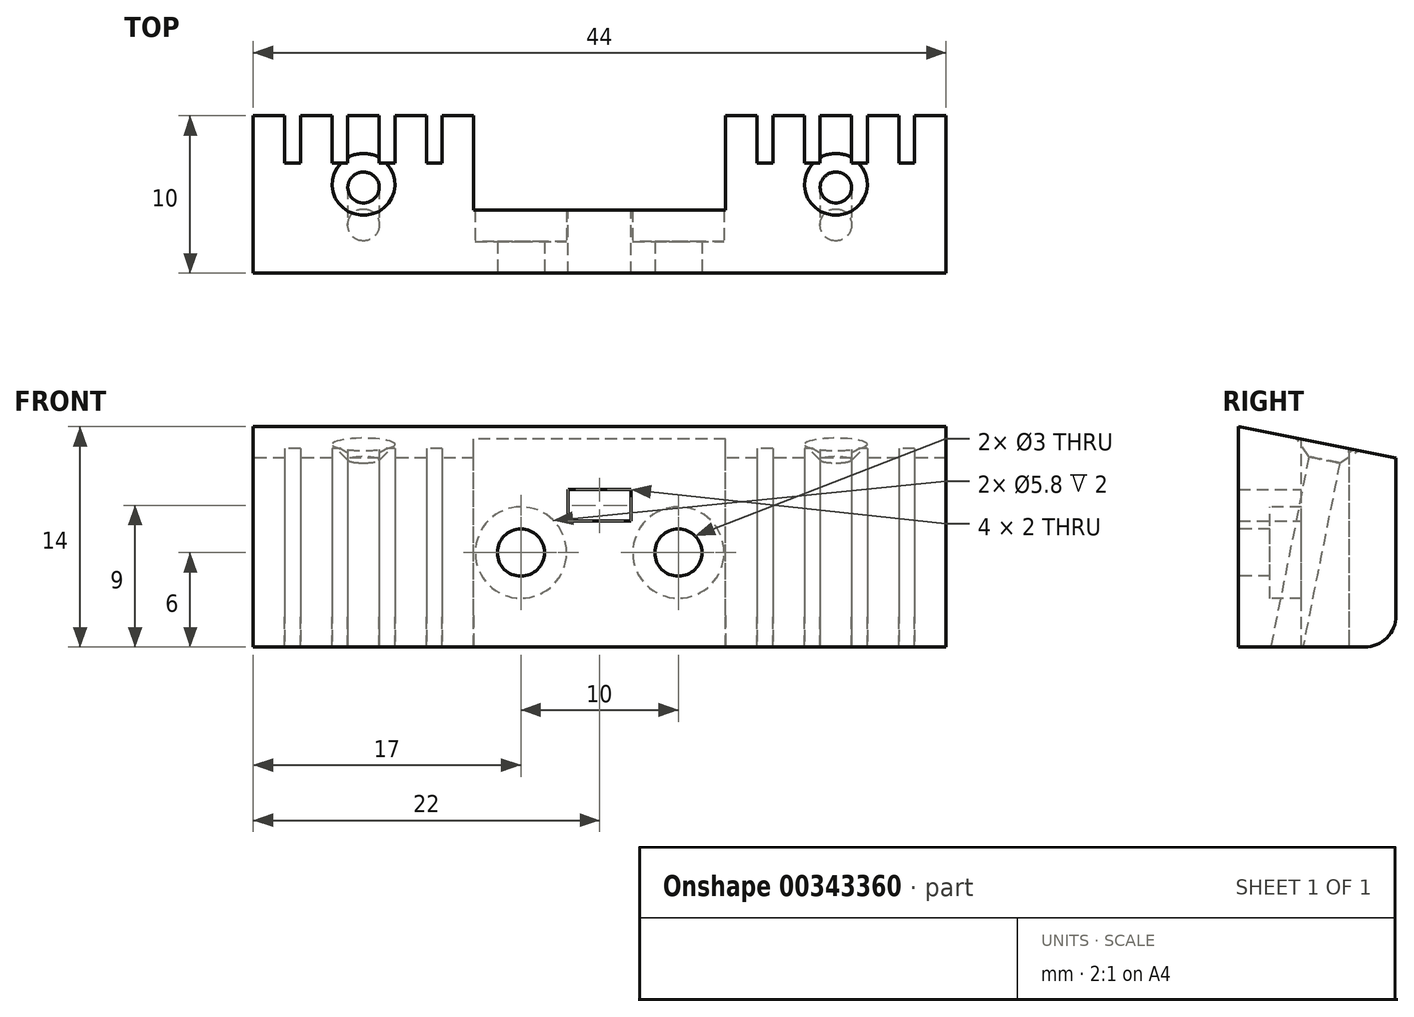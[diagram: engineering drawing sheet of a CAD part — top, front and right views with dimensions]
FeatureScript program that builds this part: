
annotation { "Feature Type Name" : "Feature", "Feature Type Description" : "" }
export const myFeature = defineFeature(function(context is Context, id is Id, definition is map)
    precondition{}
    {
        {
            var Q0;
            Q0=qCreatedBy(makeId("Right.planeOp"),FACE);
            var sketch = newSketch(context, id + "F0", { "sketchPlane" : qUnion([Q0])});
            skLineSegment(sketch, "E0.bottom", {"start": v(5, -7) * mm, "end": v(-5, -7) * mm});
            skLineSegment(sketch, "E0.top", {"start": v(5, 7) * mm, "end": v(-5, 7) * mm});
            skLineSegment(sketch, "E0.left", {"start": v(5, -7) * mm, "end": v(5, 7) * mm});
            skLineSegment(sketch, "E0.right", {"start": v(-5, -7) * mm, "end": v(-5, 7) * mm});
            skPoint(sketch, "E0.middle", {"position": v(0, 0) * mm});
            skLineSegment(sketch, "E1", {"start": v(-5, 7) * mm, "end": v(5, 5) * mm});
            skSolve(sketch);
        }
        {
            var Q0;
            {var subQ0=sQuery(id+"F0.wireOp",EDGE,"E0.bottom");Q0=makeQuery(id+"F0.imprint","IMPRINT",FACE,{"disambiguationData":[TD([[makeQuery(id+"F0.imprint","IMPRINT",EDGE,{"derivedFrom":subQ0}),-1.0]])]});}
            extrude(context, id + "F1", {"entities" : qUnion([Q0]), "depth" : 44 * mm, "symmetric" : true});
        }
        {
            var Q0;
            Q0=makeQuery(id+"F1.opExtrude","SWEPT_FACE",FACE,{"disambiguationData":[OSD([sQuery(id+"F0.wireOp",EDGE,"E0.left")])]});
            var sketch = newSketch(context, id + "F2", { "sketchPlane" : qUnion([Q0])});
            skLineSegment(sketch, "E2.bottom", {"start": v(8, -7) * mm, "end": v(-8, -7) * mm});
            skLineSegment(sketch, "E2.top", {"start": v(8, 7) * mm, "end": v(-8, 7) * mm});
            skLineSegment(sketch, "E2.left", {"start": v(8, -7) * mm, "end": v(8, 7) * mm});
            skLineSegment(sketch, "E2.right", {"start": v(-8, -7) * mm, "end": v(-8, 7) * mm});
            skPoint(sketch, "E2.middle", {"position": v(0, 0) * mm});
            skSolve(sketch);
        }
        {
            var Q0;
            {var subQ0=sQuery(id+"F2.wireOp",EDGE,"E2.bottom");Q0=makeQuery(id+"F2.imprint","IMPRINT",FACE,{"disambiguationData":[TD([[makeQuery(id+"F2.imprint","IMPRINT",EDGE,{"derivedFrom":subQ0}),1.0]])]});}
            var Q1;
            {var subQ0=sQuery(id+"F2.wireOp",EDGE,"E2.top");Q1=makeQuery(id+"F2.imprint","IMPRINT",FACE,{"disambiguationData":[TD([[makeQuery(id+"F2.imprint","IMPRINT",EDGE,{"derivedFrom":subQ0}),1.0]])]});}
            extrude(context, id + "F3", {"entities" : qUnion([Q0, Q1]), "operationType" : NewBodyOperationType.REMOVE, "oppositeDirection" : true, "depth" : 6 * mm});
        }
        {
            var Q0;
            {var subQ2=sQuery(id+"F0.wireOp",EDGE,"E0.left");Q0=makeQuery(id+"F3.boolean.opBoolean","SPLIT",FACE,{"disambiguationData":[TD([makeQuery(id+"F3.opExtrude","SWEPT_FACE",FACE,{"disambiguationData":[OSD([sQuery(id+"F2.wireOp",EDGE,"E2.left")])]})])],"derivedFrom":makeQuery(id+"F1.opExtrude","SWEPT_FACE",FACE,{"disambiguationData":[OSD([subQ2])]})});}
            var sketch = newSketch(context, id + "F4", { "sketchPlane" : qUnion([Q0])});
            skLineSegment(sketch, "E3.0", {"start": v(-22, 7) * mm, "end": v(22, 7) * mm});
            skLineSegment(sketch, "E4.bottom", {"start": v(8, 7) * mm, "end": v(10, 7) * mm});
            skLineSegment(sketch, "E4.top", {"start": v(8, -7) * mm, "end": v(10, -7) * mm});
            skLineSegment(sketch, "E4.left", {"start": v(8, 7) * mm, "end": v(8, -7) * mm});
            skLineSegment(sketch, "E4.right", {"start": v(10, 7) * mm, "end": v(10, -7) * mm});
            skLineSegment(sketch, "E5.1.0.0", {"start": v(13, 7) * mm, "end": v(13, -7) * mm});
            skLineSegment(sketch, "E5.1.0.1", {"start": v(11, 7) * mm, "end": v(13, 7) * mm});
            skLineSegment(sketch, "E5.1.0.2", {"start": v(11, 7) * mm, "end": v(11, -7) * mm});
            skLineSegment(sketch, "E5.1.0.3", {"start": v(11, -7) * mm, "end": v(13, -7) * mm});
            skLineSegment(sketch, "E5.2.0.0", {"start": v(16, 7) * mm, "end": v(16, -7) * mm});
            skLineSegment(sketch, "E5.2.0.1", {"start": v(14, 7) * mm, "end": v(16, 7) * mm});
            skLineSegment(sketch, "E5.2.0.2", {"start": v(14, 7) * mm, "end": v(14, -7) * mm});
            skLineSegment(sketch, "E5.2.0.3", {"start": v(14, -7) * mm, "end": v(16, -7) * mm});
            skLineSegment(sketch, "E5.3.0.0", {"start": v(19, 7) * mm, "end": v(19, -7) * mm});
            skLineSegment(sketch, "E5.3.0.1", {"start": v(17, 7) * mm, "end": v(19, 7) * mm});
            skLineSegment(sketch, "E5.3.0.2", {"start": v(17, 7) * mm, "end": v(17, -7) * mm});
            skLineSegment(sketch, "E5.3.0.3", {"start": v(17, -7) * mm, "end": v(19, -7) * mm});
            skLineSegment(sketch, "E5.4.0.0", {"start": v(22, 7) * mm, "end": v(22, -7) * mm});
            skLineSegment(sketch, "E5.4.0.1", {"start": v(20, 7) * mm, "end": v(22, 7) * mm});
            skLineSegment(sketch, "E5.4.0.2", {"start": v(20, 7) * mm, "end": v(20, -7) * mm});
            skLineSegment(sketch, "E5.4.0.3", {"start": v(20, -7) * mm, "end": v(22, -7) * mm});
            skLineSegment(sketch, "E5.direction1", {"start": v(8, -7) * mm, "end": v(11, -7) * mm, "construction": true});
            skLineSegment(sketch, "E6.MirrorCS", {"start": v(-8, 7) * mm, "end": v(-8, -7) * mm});
            skLineSegment(sketch, "E7.MirrorCS", {"start": v(-10, 7) * mm, "end": v(-10, -7) * mm});
            skLineSegment(sketch, "E8.MirrorCS", {"start": v(-11, 7) * mm, "end": v(-11, -7) * mm});
            skLineSegment(sketch, "E9.MirrorCS", {"start": v(-13, 7) * mm, "end": v(-13, -7) * mm});
            skLineSegment(sketch, "E10.MirrorCS", {"start": v(-14, 7) * mm, "end": v(-14, -7) * mm});
            skLineSegment(sketch, "E11.MirrorCS", {"start": v(-16, 7) * mm, "end": v(-16, -7) * mm});
            skLineSegment(sketch, "E12.MirrorCS", {"start": v(-17, 7) * mm, "end": v(-17, -7) * mm});
            skLineSegment(sketch, "E13.MirrorCS", {"start": v(-19, 7) * mm, "end": v(-19, -7) * mm});
            skLineSegment(sketch, "E14.MirrorCS", {"start": v(-20, 7) * mm, "end": v(-20, -7) * mm});
            skLineSegment(sketch, "E15.MirrorCS", {"start": v(-22, 7) * mm, "end": v(-22, -7) * mm});
            skLineSegment(sketch, "E16", {"start": v(-22, -7) * mm, "end": v(-8, -7) * mm});
            skSolve(sketch);
        }
        {
            var Q0;
            {var subQ0=sQuery(id+"F4.wireOp",EDGE,"E7.MirrorCS");Q0=makeQuery(id+"F4.imprint","IMPRINT",FACE,{"disambiguationData":[TD([[makeQuery(id+"F4.imprint","IMPRINT",EDGE,{"derivedFrom":subQ0}),-1.0]])]});}
            var Q1;
            {var subQ0=sQuery(id+"F4.wireOp",EDGE,"E9.MirrorCS");Q1=makeQuery(id+"F4.imprint","IMPRINT",FACE,{"disambiguationData":[TD([[makeQuery(id+"F4.imprint","IMPRINT",EDGE,{"derivedFrom":subQ0}),-1.0]])]});}
            var Q2;
            {var subQ0=sQuery(id+"F4.wireOp",EDGE,"E11.MirrorCS");Q2=makeQuery(id+"F4.imprint","IMPRINT",FACE,{"disambiguationData":[TD([[makeQuery(id+"F4.imprint","IMPRINT",EDGE,{"derivedFrom":subQ0}),-1.0]])]});}
            var Q3;
            {var subQ0=sQuery(id+"F4.wireOp",EDGE,"E13.MirrorCS");Q3=makeQuery(id+"F4.imprint","IMPRINT",FACE,{"disambiguationData":[TD([[makeQuery(id+"F4.imprint","IMPRINT",EDGE,{"derivedFrom":subQ0}),-1.0]])]});}
            var Q4;
            {var subQ0=sQuery(id+"F4.wireOp",EDGE,"E4.right");var subQ2=sQuery(id+"F0.wireOp",EDGE,"E1");var subQ3=sQuery(id+"F0.wireOp",EDGE,"E0.left");var subQ6=makeQuery(id+"F3.opExtrude","SWEPT_FACE",FACE,{"disambiguationData":[OSD([sQuery(id+"F2.wireOp",EDGE,"E2.left")])]});var subQ9=makeQuery(id+"F3.boolean.opBoolean","SPLIT",EDGE,{"disambiguationData":[TD([subQ6])],"derivedFrom":makeQuery(id+"F1.opExtrude","SWEPT_EDGE",EDGE,{"disambiguationData":[OSD([subQ3,subQ2])]})});var subQ10=makeQuery(id+"F4.imprint","INTERSECT",VERTEX,{"derivedFrom":[subQ9,subQ0]});Q4=makeQuery(id+"F4.imprint","IMPRINT",FACE,{"disambiguationData":[TD([[makeQuery(id+"F4.imprint","IMPRINT",EDGE,{"disambiguationData":[TD([[subQ10,-1.0]])],"derivedFrom":subQ0}),1.0]])]});}
            var Q5;
            {var subQ0=sQuery(id+"F4.wireOp",EDGE,"E5.1.0.0");var subQ2=sQuery(id+"F0.wireOp",EDGE,"E1");var subQ3=sQuery(id+"F0.wireOp",EDGE,"E0.left");var subQ6=makeQuery(id+"F3.opExtrude","SWEPT_FACE",FACE,{"disambiguationData":[OSD([sQuery(id+"F2.wireOp",EDGE,"E2.left")])]});var subQ9=makeQuery(id+"F3.boolean.opBoolean","SPLIT",EDGE,{"disambiguationData":[TD([subQ6])],"derivedFrom":makeQuery(id+"F1.opExtrude","SWEPT_EDGE",EDGE,{"disambiguationData":[OSD([subQ3,subQ2])]})});var subQ10=makeQuery(id+"F4.imprint","INTERSECT",VERTEX,{"derivedFrom":[subQ9,subQ0]});Q5=makeQuery(id+"F4.imprint","IMPRINT",FACE,{"disambiguationData":[TD([[makeQuery(id+"F4.imprint","IMPRINT",EDGE,{"disambiguationData":[TD([[subQ10,-1.0]])],"derivedFrom":subQ0}),1.0]])]});}
            var Q6;
            {var subQ0=sQuery(id+"F4.wireOp",EDGE,"E5.2.0.0");var subQ2=sQuery(id+"F0.wireOp",EDGE,"E1");var subQ3=sQuery(id+"F0.wireOp",EDGE,"E0.left");var subQ6=makeQuery(id+"F3.opExtrude","SWEPT_FACE",FACE,{"disambiguationData":[OSD([sQuery(id+"F2.wireOp",EDGE,"E2.left")])]});var subQ9=makeQuery(id+"F3.boolean.opBoolean","SPLIT",EDGE,{"disambiguationData":[TD([subQ6])],"derivedFrom":makeQuery(id+"F1.opExtrude","SWEPT_EDGE",EDGE,{"disambiguationData":[OSD([subQ3,subQ2])]})});var subQ10=makeQuery(id+"F4.imprint","INTERSECT",VERTEX,{"derivedFrom":[subQ9,subQ0]});Q6=makeQuery(id+"F4.imprint","IMPRINT",FACE,{"disambiguationData":[TD([[makeQuery(id+"F4.imprint","IMPRINT",EDGE,{"disambiguationData":[TD([[subQ10,-1.0]])],"derivedFrom":subQ0}),1.0]])]});}
            var Q7;
            {var subQ0=sQuery(id+"F4.wireOp",EDGE,"E5.3.0.0");var subQ2=sQuery(id+"F0.wireOp",EDGE,"E1");var subQ3=sQuery(id+"F0.wireOp",EDGE,"E0.left");var subQ6=makeQuery(id+"F3.opExtrude","SWEPT_FACE",FACE,{"disambiguationData":[OSD([sQuery(id+"F2.wireOp",EDGE,"E2.left")])]});var subQ9=makeQuery(id+"F3.boolean.opBoolean","SPLIT",EDGE,{"disambiguationData":[TD([subQ6])],"derivedFrom":makeQuery(id+"F1.opExtrude","SWEPT_EDGE",EDGE,{"disambiguationData":[OSD([subQ3,subQ2])]})});var subQ10=makeQuery(id+"F4.imprint","INTERSECT",VERTEX,{"derivedFrom":[subQ9,subQ0]});Q7=makeQuery(id+"F4.imprint","IMPRINT",FACE,{"disambiguationData":[TD([[makeQuery(id+"F4.imprint","IMPRINT",EDGE,{"disambiguationData":[TD([[subQ10,-1.0]])],"derivedFrom":subQ0}),1.0]])]});}
            var Q8;
            {var subQ0=sQuery(id+"F4.wireOp",EDGE,"E5.4.0.2");var subQ1=sQuery(id+"F4.wireOp",EDGE,"E3.0");var subQ2=makeQuery(id+"F4.imprint","INTERSECT",VERTEX,{"derivedFrom":[subQ1,sQuery(id+"F4.wireOp",EDGE,"E5.4.0.1"),subQ0]});Q8=makeQuery(id+"F4.imprint","IMPRINT",FACE,{"disambiguationData":[TD([[makeQuery(id+"F4.imprint","IMPRINT",EDGE,{"disambiguationData":[TD([[subQ2,1.0]])],"derivedFrom":subQ1}),-1.0]])]});}
            var Q9;
            {var subQ0=sQuery(id+"F4.wireOp",EDGE,"E5.2.0.0");var subQ1=sQuery(id+"F4.wireOp",EDGE,"E3.0");var subQ2=makeQuery(id+"F4.imprint","INTERSECT",VERTEX,{"derivedFrom":[subQ1,subQ0,sQuery(id+"F4.wireOp",EDGE,"E5.2.0.1")]});Q9=makeQuery(id+"F4.imprint","IMPRINT",FACE,{"disambiguationData":[TD([[makeQuery(id+"F4.imprint","IMPRINT",EDGE,{"disambiguationData":[TD([[subQ2,-1.0]])],"derivedFrom":subQ1}),-1.0]])]});}
            var Q10;
            {var subQ0=sQuery(id+"F4.wireOp",EDGE,"E5.1.0.0");var subQ1=sQuery(id+"F4.wireOp",EDGE,"E3.0");var subQ2=makeQuery(id+"F4.imprint","INTERSECT",VERTEX,{"derivedFrom":[subQ1,subQ0,sQuery(id+"F4.wireOp",EDGE,"E5.1.0.1")]});Q10=makeQuery(id+"F4.imprint","IMPRINT",FACE,{"disambiguationData":[TD([[makeQuery(id+"F4.imprint","IMPRINT",EDGE,{"disambiguationData":[TD([[subQ2,-1.0]])],"derivedFrom":subQ1}),-1.0]])]});}
            var Q11;
            {var subQ0=sQuery(id+"F4.wireOp",EDGE,"E4.right");var subQ1=sQuery(id+"F4.wireOp",EDGE,"E3.0");var subQ2=makeQuery(id+"F4.imprint","INTERSECT",VERTEX,{"derivedFrom":[subQ1,sQuery(id+"F4.wireOp",EDGE,"E4.bottom"),subQ0]});Q11=makeQuery(id+"F4.imprint","IMPRINT",FACE,{"disambiguationData":[TD([[makeQuery(id+"F4.imprint","IMPRINT",EDGE,{"disambiguationData":[TD([[subQ2,-1.0]])],"derivedFrom":subQ1}),-1.0]])]});}
            extrude(context, id + "F5", {"entities" : qUnion([Q0, Q1, Q2, Q3, Q4, Q5, Q6, Q7, Q8, Q9, Q10, Q11]), "operationType" : NewBodyOperationType.REMOVE, "oppositeDirection" : true, "depth" : 3 * mm});
        }
        {
            var Q0;
            {var subQ0=sQuery(id+"F0.wireOp",EDGE,"E0.bottom");var subQ2=sQuery(id+"F0.wireOp",EDGE,"E0.left");Q0=makeQuery(id+"F5.boolean.opBoolean","SPLIT",EDGE,{"disambiguationData":[TD([makeQuery(id+"F5.opExtrude","SWEPT_FACE",FACE,{"disambiguationData":[OSD([sQuery(id+"F4.wireOp",EDGE,"E14.MirrorCS")])]})])],"derivedFrom":makeQuery(id+"F3.boolean.opBoolean","SPLIT",EDGE,{"disambiguationData":[TD([makeQuery(id+"F3.opExtrude","SWEPT_FACE",FACE,{"disambiguationData":[OSD([sQuery(id+"F2.wireOp",EDGE,"E2.right")])]})])],"derivedFrom":makeQuery(id+"F1.opExtrude","SWEPT_EDGE",EDGE,{"disambiguationData":[OSD([subQ0,subQ2])]})})});}
            var Q1;
            {var subQ0=sQuery(id+"F0.wireOp",EDGE,"E0.bottom");var subQ2=sQuery(id+"F0.wireOp",EDGE,"E0.left");Q1=makeQuery(id+"F5.boolean.opBoolean","SPLIT",EDGE,{"disambiguationData":[TD([makeQuery(id+"F5.opExtrude","SWEPT_FACE",FACE,{"disambiguationData":[OSD([sQuery(id+"F4.wireOp",EDGE,"E12.MirrorCS")])]})])],"derivedFrom":makeQuery(id+"F3.boolean.opBoolean","SPLIT",EDGE,{"disambiguationData":[TD([makeQuery(id+"F3.opExtrude","SWEPT_FACE",FACE,{"disambiguationData":[OSD([sQuery(id+"F2.wireOp",EDGE,"E2.right")])]})])],"derivedFrom":makeQuery(id+"F1.opExtrude","SWEPT_EDGE",EDGE,{"disambiguationData":[OSD([subQ0,subQ2])]})})});}
            var Q2;
            {var subQ0=sQuery(id+"F0.wireOp",EDGE,"E0.bottom");var subQ2=sQuery(id+"F0.wireOp",EDGE,"E0.left");Q2=makeQuery(id+"F5.boolean.opBoolean","SPLIT",EDGE,{"disambiguationData":[TD([makeQuery(id+"F5.opExtrude","SWEPT_FACE",FACE,{"disambiguationData":[OSD([sQuery(id+"F4.wireOp",EDGE,"E10.MirrorCS")])]})])],"derivedFrom":makeQuery(id+"F3.boolean.opBoolean","SPLIT",EDGE,{"disambiguationData":[TD([makeQuery(id+"F3.opExtrude","SWEPT_FACE",FACE,{"disambiguationData":[OSD([sQuery(id+"F2.wireOp",EDGE,"E2.right")])]})])],"derivedFrom":makeQuery(id+"F1.opExtrude","SWEPT_EDGE",EDGE,{"disambiguationData":[OSD([subQ0,subQ2])]})})});}
            var Q3;
            {var subQ0=sQuery(id+"F0.wireOp",EDGE,"E0.bottom");var subQ2=sQuery(id+"F0.wireOp",EDGE,"E0.left");Q3=makeQuery(id+"F5.boolean.opBoolean","SPLIT",EDGE,{"disambiguationData":[TD([makeQuery(id+"F5.opExtrude","SWEPT_FACE",FACE,{"disambiguationData":[OSD([sQuery(id+"F4.wireOp",EDGE,"E8.MirrorCS")])]})])],"derivedFrom":makeQuery(id+"F3.boolean.opBoolean","SPLIT",EDGE,{"disambiguationData":[TD([makeQuery(id+"F3.opExtrude","SWEPT_FACE",FACE,{"disambiguationData":[OSD([sQuery(id+"F2.wireOp",EDGE,"E2.right")])]})])],"derivedFrom":makeQuery(id+"F1.opExtrude","SWEPT_EDGE",EDGE,{"disambiguationData":[OSD([subQ0,subQ2])]})})});}
            var Q4;
            {var subQ0=sQuery(id+"F0.wireOp",EDGE,"E0.bottom");var subQ2=sQuery(id+"F0.wireOp",EDGE,"E0.left");var subQ4=makeQuery(id+"F3.opExtrude","SWEPT_FACE",FACE,{"disambiguationData":[OSD([sQuery(id+"F2.wireOp",EDGE,"E2.right")])]});Q4=makeQuery(id+"F5.boolean.opBoolean","SPLIT",EDGE,{"disambiguationData":[TD([makeQuery(id+"F3.boolean.opBoolean","COPY",FACE,{"derivedFrom":subQ4})])],"derivedFrom":makeQuery(id+"F3.boolean.opBoolean","SPLIT",EDGE,{"disambiguationData":[TD([subQ4])],"derivedFrom":makeQuery(id+"F1.opExtrude","SWEPT_EDGE",EDGE,{"disambiguationData":[OSD([subQ0,subQ2])]})})});}
            var Q5;
            {var subQ0=sQuery(id+"F0.wireOp",EDGE,"E0.bottom");var subQ2=makeQuery(id+"F3.opExtrude","SWEPT_FACE",FACE,{"disambiguationData":[OSD([sQuery(id+"F2.wireOp",EDGE,"E2.left")])]});var subQ3=sQuery(id+"F0.wireOp",EDGE,"E0.left");Q5=makeQuery(id+"F5.boolean.opBoolean","SPLIT",EDGE,{"disambiguationData":[TD([makeQuery(id+"F3.boolean.opBoolean","COPY",FACE,{"derivedFrom":subQ2})])],"derivedFrom":makeQuery(id+"F3.boolean.opBoolean","SPLIT",EDGE,{"disambiguationData":[TD([subQ2])],"derivedFrom":makeQuery(id+"F1.opExtrude","SWEPT_EDGE",EDGE,{"disambiguationData":[OSD([subQ0,subQ3])]})})});}
            var Q6;
            {var subQ0=sQuery(id+"F0.wireOp",EDGE,"E0.bottom");var subQ2=sQuery(id+"F0.wireOp",EDGE,"E0.left");Q6=makeQuery(id+"F5.boolean.opBoolean","SPLIT",EDGE,{"disambiguationData":[TD([makeQuery(id+"F5.opExtrude","SWEPT_FACE",FACE,{"disambiguationData":[OSD([sQuery(id+"F4.wireOp",EDGE,"E5.1.0.0")])]})])],"derivedFrom":makeQuery(id+"F3.boolean.opBoolean","SPLIT",EDGE,{"disambiguationData":[TD([makeQuery(id+"F3.opExtrude","SWEPT_FACE",FACE,{"disambiguationData":[OSD([sQuery(id+"F2.wireOp",EDGE,"E2.left")])]})])],"derivedFrom":makeQuery(id+"F1.opExtrude","SWEPT_EDGE",EDGE,{"disambiguationData":[OSD([subQ0,subQ2])]})})});}
            var Q7;
            {var subQ0=sQuery(id+"F0.wireOp",EDGE,"E0.bottom");var subQ2=sQuery(id+"F0.wireOp",EDGE,"E0.left");Q7=makeQuery(id+"F5.boolean.opBoolean","SPLIT",EDGE,{"disambiguationData":[TD([makeQuery(id+"F5.opExtrude","SWEPT_FACE",FACE,{"disambiguationData":[OSD([sQuery(id+"F4.wireOp",EDGE,"E5.2.0.0")])]})])],"derivedFrom":makeQuery(id+"F3.boolean.opBoolean","SPLIT",EDGE,{"disambiguationData":[TD([makeQuery(id+"F3.opExtrude","SWEPT_FACE",FACE,{"disambiguationData":[OSD([sQuery(id+"F2.wireOp",EDGE,"E2.left")])]})])],"derivedFrom":makeQuery(id+"F1.opExtrude","SWEPT_EDGE",EDGE,{"disambiguationData":[OSD([subQ0,subQ2])]})})});}
            var Q8;
            {var subQ0=sQuery(id+"F0.wireOp",EDGE,"E0.bottom");var subQ2=sQuery(id+"F0.wireOp",EDGE,"E0.left");Q8=makeQuery(id+"F5.boolean.opBoolean","SPLIT",EDGE,{"disambiguationData":[TD([makeQuery(id+"F5.opExtrude","SWEPT_FACE",FACE,{"disambiguationData":[OSD([sQuery(id+"F4.wireOp",EDGE,"E5.3.0.0")])]})])],"derivedFrom":makeQuery(id+"F3.boolean.opBoolean","SPLIT",EDGE,{"disambiguationData":[TD([makeQuery(id+"F3.opExtrude","SWEPT_FACE",FACE,{"disambiguationData":[OSD([sQuery(id+"F2.wireOp",EDGE,"E2.left")])]})])],"derivedFrom":makeQuery(id+"F1.opExtrude","SWEPT_EDGE",EDGE,{"disambiguationData":[OSD([subQ0,subQ2])]})})});}
            var Q9;
            {var subQ0=sQuery(id+"F0.wireOp",EDGE,"E0.bottom");var subQ2=sQuery(id+"F0.wireOp",EDGE,"E0.left");Q9=makeQuery(id+"F5.boolean.opBoolean","SPLIT",EDGE,{"disambiguationData":[TD([makeQuery(id+"F5.opExtrude","SWEPT_FACE",FACE,{"disambiguationData":[OSD([sQuery(id+"F4.wireOp",EDGE,"E5.4.0.2")])]})])],"derivedFrom":makeQuery(id+"F3.boolean.opBoolean","SPLIT",EDGE,{"disambiguationData":[TD([makeQuery(id+"F3.opExtrude","SWEPT_FACE",FACE,{"disambiguationData":[OSD([sQuery(id+"F2.wireOp",EDGE,"E2.left")])]})])],"derivedFrom":makeQuery(id+"F1.opExtrude","SWEPT_EDGE",EDGE,{"disambiguationData":[OSD([subQ0,subQ2])]})})});}
            fillet(context, id + "F6", {"entities" : qUnion([Q0, Q1, Q2, Q3, Q4, Q5, Q6, Q7, Q8, Q9]), "radius" : 2 * mm, "tangentPropagation" : true, "allowEdgeOverflow" : false});
        }
        {
            var Q0;
            Q0=makeQuery(id+"F1.opExtrude","SWEPT_FACE",FACE,{"disambiguationData":[OSD([sQuery(id+"F0.wireOp",EDGE,"E1")])]});
            var sketch = newSketch(context, id + "F7", { "sketchPlane" : qUnion([Q0])});
            skLineSegment(sketch, "E17", {"start": v(16, 0.86) * mm, "end": v(14, 0.86) * mm});
            skPoint(sketch, "E18", {"position": v(15, -0.53) * mm});
            skPoint(sketch, "E18.positionSnap0", {"position": v(15, 0.86) * mm});
            skPoint(sketch, "E19.MirrorP", {"position": v(-15, -0.53) * mm});
            skSolve(sketch);
        }
        {
            var Q0;
            Q0=sQuery(id+"F7.wireOp",VERTEX,"E18");
            var Q1;
            Q1=sQuery(id+"F7.wireOp",VERTEX,"E19.MirrorP");
            var Q2;
            Q2=makeQuery(id+"F1.opExtrude","SWEPT_BODY",BODY,{"disambiguationData":[OSD([sQuery(id+"F0.wireOp",EDGE,"E0.bottom"),sQuery(id+"F0.wireOp",EDGE,"E0.left"),sQuery(id+"F0.wireOp",EDGE,"E0.right"),sQuery(id+"F0.wireOp",EDGE,"E1")])]});
            hole(context, id + "F8", {"style" : HoleStyle.C_SINK, "endStyle" : HoleEndStyle.BLIND, "holeDiameter" : 2 * mm, "cSinkDiameter" : 4 * mm, "cSinkAngle" : 90 * degree, "holeDepth" : 15 * mm, "isTappedThrough" : true, "tappedDepth" : 12 * mm, "tapClearance" : 3, "locations" : qUnion([Q0, Q1]), "scope" : qUnion([Q2]), "startStyle" : HoleStartStyle.SKETCH});
        }
        {
            var Q0;
            Q0=makeQuery(id+"F3.boolean.opBoolean","COPY",FACE,{"derivedFrom":makeQuery(id+"F3.opExtrude","CAP_FACE",FACE,{"disambiguationData":[OSD([sQuery(id+"F2.wireOp",EDGE,"E2.bottom"),sQuery(id+"F2.wireOp",EDGE,"E2.top"),sQuery(id+"F2.wireOp",EDGE,"E2.left"),sQuery(id+"F2.wireOp",EDGE,"E2.right")])],"isStart":false})});
            var sketch = newSketch(context, id + "F9", { "sketchPlane" : qUnion([Q0])});
            skPoint(sketch, "E20", {"position": v(-5, -1) * mm});
            skPoint(sketch, "E21.MirrorP", {"position": v(5, -1) * mm});
            skLineSegment(sketch, "E22.bottom", {"start": v(2, 1) * mm, "end": v(-2, 1) * mm});
            skLineSegment(sketch, "E22.top", {"start": v(2, 3) * mm, "end": v(-2, 3) * mm});
            skLineSegment(sketch, "E22.left", {"start": v(2, 1) * mm, "end": v(2, 3) * mm});
            skLineSegment(sketch, "E22.right", {"start": v(-2, 1) * mm, "end": v(-2, 3) * mm});
            skPoint(sketch, "E22.middle", {"position": v(0, 2) * mm});
            skSolve(sketch);
        }
        {
            var Q0;
            Q0=makeQuery(id+"F9.imprint","IMPRINT",FACE,{"disambiguationData":[TD([[makeQuery(id+"F9.imprint","IMPRINT",EDGE,{"derivedFrom":sQuery(id+"F9.wireOp",EDGE,"E22.bottom")}),-1.0]])]});
            extrude(context, id + "F10", {"entities" : qUnion([Q0]), "operationType" : NewBodyOperationType.REMOVE, "oppositeDirection" : true, "depth" : 25 * mm});
        }
        {
            var Q0;
            Q0=sQuery(id+"F9.wireOp",VERTEX,"E20");
            var Q1;
            Q1=sQuery(id+"F9.wireOp",VERTEX,"E21.MirrorP");
            var Q2;
            Q2=makeQuery(id+"F1.opExtrude","SWEPT_BODY",BODY,{"disambiguationData":[OSD([sQuery(id+"F0.wireOp",EDGE,"E0.bottom"),sQuery(id+"F0.wireOp",EDGE,"E0.left"),sQuery(id+"F0.wireOp",EDGE,"E0.right"),sQuery(id+"F0.wireOp",EDGE,"E1")])]});
            hole(context, id + "F11", {"style" : HoleStyle.C_BORE, "endStyle" : HoleEndStyle.BLIND, "holeDiameter" : 3 * mm, "cBoreDiameter" : 5.8 * mm, "cBoreDepth" : 2 * mm, "holeDepth" : 15 * mm, "isTappedThrough" : true, "tappedDepth" : 12 * mm, "tapClearance" : 3, "locations" : qUnion([Q0, Q1]), "scope" : qUnion([Q2]), "startStyle" : HoleStartStyle.SKETCH});
        }
    });
